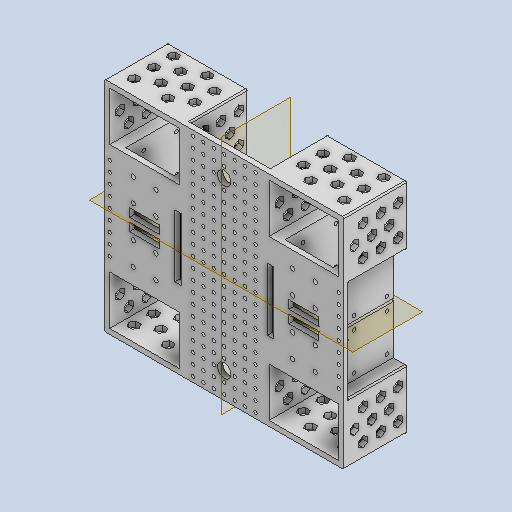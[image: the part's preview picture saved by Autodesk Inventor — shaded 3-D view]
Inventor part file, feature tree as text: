
AUTODESK INVENTOR PART (.ipt)
format: ipt  version: 2024.2 (Build 282272000, 272)  size: 1,509,376 bytes
history: native  units: mm
features: other x27, sketch x11, extrude x10, mirror x6, fillet x2, projected_geometry x1
ambient origin geometry x8: Origin, YZ Plane, XZ Plane, XY Plane, X Axis, Y Axis, Z Axis, Center Point
bodies: Body1 (feature_tree)
feature tree (57):
  extrude  "Extrusion2"  Depth=5.0mm
  sketch  "Esquisse3"
  other  "Plan de construction1"
  extrude  "Extrusion3"  Depth=5.0mm
  other  "Epaississement1"
  other  "Epaississement2"
  extrude  "Extrusion6"  Depth=5.0mm
  fillet  "Congé1"  Radius=5.0mm
  fillet  "Congé2"  Radius=5.0mm
  extrude  "Extrusion8"  Depth=5.0mm
  sketch  "Esquisse9"
  extrude  "Extrusion9"  Depth=5.0mm
  extrude  "Extrusion10"  Depth=5.0mm
  extrude  "Extrusion11"  Depth=3.0mm
  mirror  "Symétrie1"
  mirror  "Symétrie2"
  extrude  "Extrusion12"  Depth=3.0mm
  mirror  "Symétrie3"
  mirror  "Symétrie4"
  extrude  "Extrusion13"  Depth=50.25mm TaperAngle=0.0deg
  mirror  "Symétrie5"
  extrude  "Extrusion14"  Depth=0.15mm
  mirror  "Symétrie6"
  sketch  "Esquisse1"
  other  "Référence1"
  other  "Référence2"
  other  "Référence3"
  other  "Référence4"
  other  "Référence5"
  other  "Référence6"
  other  "Référence7"
  other  "Référence8"
  projected_geometry  "Boucle projetée1"
  sketch  "Esquisse6"
  other  "Référence9"
  other  "Référence10"
  sketch  "Esquisse8"
  other  "Référence15"
  other  "Référence16"
  other  "Référence17"
  other  "Référence18"
  other  "Référence19"
  other  "Référence20"
  sketch  "Esquisse10"
  sketch  "Esquisse11"
  sketch  "Esquisse12"
  other  "Référence21"
  other  "Plan de construction2"
  other  "Plan de construction3"
  other  "Plan de construction4"
  sketch  "Esquisse13"
  sketch  "Esquisse14"
  sketch  "Esquisse15"
  other  "<userpath>\Desktop\Robot\Robotbebou.iam"
  other  "Robotbebou.iam"
  other  "embase_pla:1"
  other  "SF2423-10B41:2"
